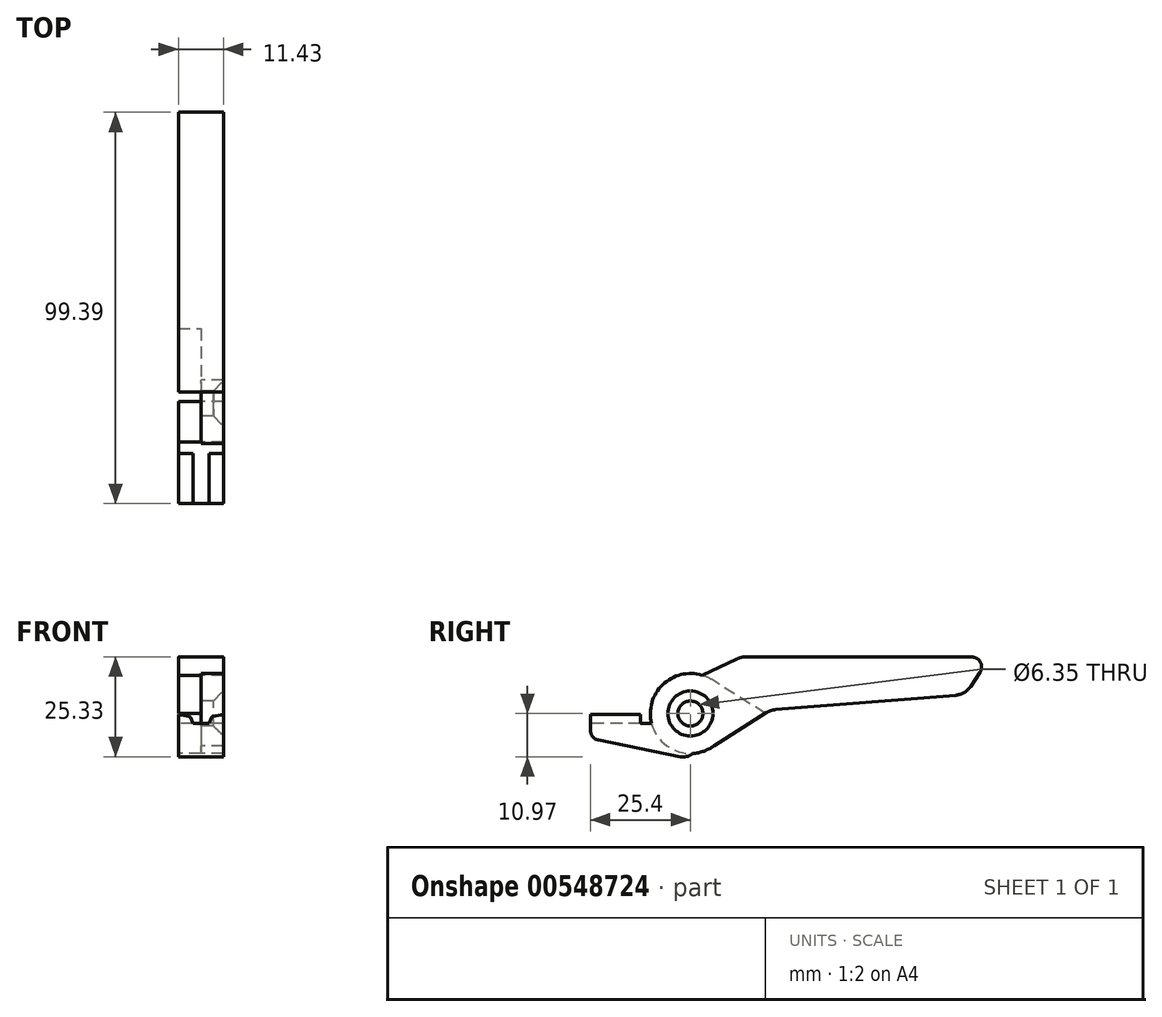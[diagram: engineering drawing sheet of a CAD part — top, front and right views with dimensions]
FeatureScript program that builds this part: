
annotation { "Feature Type Name" : "Feature", "Feature Type Description" : "" }
export const myFeature = defineFeature(function(context is Context, id is Id, definition is map)
    precondition{}
    {
        {
            var Q0;
            Q0=qCreatedBy(makeId("Right.planeOp"),FACE);
            var sketch = newSketch(context, id + "F0", { "sketchPlane" : qUnion([Q0])});
            skCircle(sketch, "E0", {"center": v(0, 0) * mm, "radius": 3.18 * mm});
            skCircle(sketch, "E1", {"center": v(0, 0) * mm, "radius": 10.16 * mm});
            skSolve(sketch);
        }
        {
            var Q0;
            Q0=qCreatedBy(makeId("Right.planeOp"),FACE);
            var sketch = newSketch(context, id + "F1", { "sketchPlane" : qUnion([Q0])});
            skLineSegment(sketch, "E2", {"start": v(9.3, 0) * mm, "end": v(10.16, 0.07) * mm});
            skLineSegment(sketch, "E3", {"start": v(69.85, 4.85) * mm, "end": v(76.2, 14.36) * mm});
            skCircle(sketch, "E4", {"center": v(0, 0) * mm, "radius": 10.16 * mm, "construction": true});
            skLineSegment(sketch, "E5", {"start": v(0, 0) * mm, "end": v(76.2, 0) * mm, "construction": true});
            skLineSegment(sketch, "E6", {"start": v(76.2, 14.36) * mm, "end": v(12.8, 14.36) * mm});
            skLineSegment(sketch, "E7", {"start": v(12.8, 14.36) * mm, "end": v(2.92, 9.73) * mm});
            skLineSegment(sketch, "E8", {"start": v(76.2, 14.36) * mm, "end": v(76.2, 0) * mm, "construction": true});
            skPoint(sketch, "E9.endSnap0", {"position": v(7.86, 12.04) * mm});
            skLineSegment(sketch, "E10", {"start": v(5.96, -8.23) * mm, "end": v(4.87, -6.63) * mm});
            skLineSegment(sketch, "E11", {"start": v(4.87, -6.63) * mm, "end": v(8.24, 1.75) * mm});
            skLineSegment(sketch, "E12", {"start": v(8.24, 1.75) * mm, "end": v(2.92, 9.73) * mm});
            skLineSegment(sketch, "E13.trimOffspring", {"start": v(20.4, 0.89) * mm, "end": v(69.85, 4.85) * mm});
            skLineSegment(sketch, "E14", {"start": v(20.4, 0.89) * mm, "end": v(5.96, -8.23) * mm});
            skSolve(sketch);
        }
        {
            var Q0;
            Q0=qSketchRegion(id+"F1",true);
            extrude(context, id + "F2", {"entities" : qUnion([Q0]), "endBound" : BoundingType.SYMMETRIC, "depth" : 11.43 * mm, "offsetDistance" : 25.4 * mm});
        }
        {
            var Q0;
            Q0=makeQuery(id+"F2.opExtrude","SWEPT_EDGE",EDGE,{"disambiguationData":[OSD([sQuery(id+"F1.wireOp",EDGE,"E6"),sQuery(id+"F1.wireOp",EDGE,"E7")])]});
            var Q1;
            Q1=makeQuery(id+"F2.opExtrude","SWEPT_EDGE",EDGE,{"disambiguationData":[OSD([sQuery(id+"F1.wireOp",EDGE,"E3"),sQuery(id+"F1.wireOp",EDGE,"E13.trimOffspring")])]});
            var Q2;
            Q2=makeQuery(id+"F2.opExtrude","SWEPT_EDGE",EDGE,{"disambiguationData":[OSD([sQuery(id+"F1.wireOp",EDGE,"E13.trimOffspring"),sQuery(id+"F1.wireOp",EDGE,"E14")])]});
            fillet(context, id + "F3", {"entities" : qUnion([Q0, Q1, Q2]), "radius" : 5.08 * mm, "tangentPropagation" : true, "allowEdgeOverflow" : false});
        }
        {
            var Q0;
            Q0=makeQuery(id+"F2.opExtrude","SWEPT_EDGE",EDGE,{"disambiguationData":[OSD([sQuery(id+"F1.wireOp",EDGE,"E3"),sQuery(id+"F1.wireOp",EDGE,"E6")])]});
            fillet(context, id + "F4", {"entities" : qUnion([Q0]), "radius" : 2.54 * mm, "tangentPropagation" : true, "allowEdgeOverflow" : false});
        }
        {
            var Q0;
            Q0=qSketchRegion(id+"F0",true);
            extrude(context, id + "F5", {"entities" : qUnion([Q0]), "operationType" : NewBodyOperationType.ADD, "depth" : 5.7 * mm, "offsetDistance" : 25.4 * mm});
        }
        {
            var Q0;
            Q0=qCreatedBy(makeId("Right.planeOp"),FACE);
            var sketch = newSketch(context, id + "F6", { "sketchPlane" : qUnion([Q0])});
            skArc(sketch, "E15", {"start": v(5.42, 8.6) * mm, "mid": v(-10.16, -0.1) * mm, "end": v(5.57, -8.5) * mm});
            skLineSegment(sketch, "E16", {"start": v(19.06, 0) * mm, "end": v(5.42, 8.6) * mm});
            skLineSegment(sketch, "E17", {"start": v(5.57, -8.5) * mm, "end": v(19.06, 0) * mm});
            skSolve(sketch);
        }
        {
            var Q0;
            Q0=qSketchRegion(id+"F6",true);
            extrude(context, id + "F7", {"entities" : qUnion([Q0]), "operationType" : NewBodyOperationType.REMOVE, "oppositeDirection" : true, "depth" : 25.4 * mm, "offsetDistance" : 25.4 * mm});
        }
        {
            var Q0;
            Q0=qCreatedBy(makeId("Right.planeOp"),FACE);
            var sketch = newSketch(context, id + "F8", { "sketchPlane" : qUnion([Q0])});
            skCircle(sketch, "E18", {"center": v(0, 0) * mm, "radius": 10.16 * mm});
            skLineSegment(sketch, "E19", {"start": v(-9.84, 2.54) * mm, "end": v(-25.4, 2.54) * mm});
            skLineSegment(sketch, "E20", {"start": v(-25.4, 2.54) * mm, "end": v(-25.4, 6.36) * mm});
            skLineSegment(sketch, "E21", {"start": v(-25.4, 6.36) * mm, "end": v(-2.53, 10.97) * mm});
            skLineSegment(sketch, "E22", {"start": v(-2.53, 10.97) * mm, "end": v(7.5, 10.97) * mm});
            skLineSegment(sketch, "E23", {"start": v(7.5, 10.97) * mm, "end": v(4.02, 9.33) * mm});
            skLineSegment(sketch, "E24", {"start": v(0, 0) * mm, "end": v(-31.38, 0) * mm, "construction": true});
            skLineSegment(sketch, "E25.MirrorCS", {"start": v(-9.84, -2.54) * mm, "end": v(-25.4, -2.54) * mm});
            skLineSegment(sketch, "E26.MirrorCS", {"start": v(-25.4, -2.54) * mm, "end": v(-25.4, -6.36) * mm});
            skLineSegment(sketch, "E27.MirrorCS", {"start": v(-25.4, -6.36) * mm, "end": v(-2.53, -10.97) * mm});
            skLineSegment(sketch, "E28.MirrorCS", {"start": v(-2.53, -10.97) * mm, "end": v(7.5, -10.97) * mm});
            skLineSegment(sketch, "E29.MirrorCS", {"start": v(7.5, -10.97) * mm, "end": v(4.02, -9.33) * mm});
            skLineSegment(sketch, "E30", {"start": v(0.54, -10.15) * mm, "end": v(0.54, -10.97) * mm});
            skSolve(sketch);
        }
        {
            var Q0;
            {var subQ0=sQuery(id+"F8.wireOp",EDGE,"E25.MirrorCS");Q0=makeQuery(id+"F8.imprint","IMPRINT",FACE,{"disambiguationData":[TD([[makeQuery(id+"F8.imprint","IMPRINT",EDGE,{"derivedFrom":subQ0}),1.0]])]});}
            extrude(context, id + "F9", {"entities" : qUnion([Q0]), "operationType" : NewBodyOperationType.ADD, "endBound" : BoundingType.SYMMETRIC, "depth" : 11.43 * mm, "offsetDistance" : 25.4 * mm});
        }
        {
            var Q0;
            Q0=makeQuery(id+"F9.opExtrude","SWEPT_EDGE",EDGE,{"disambiguationData":[OSD([sQuery(id+"F8.wireOp",EDGE,"E28.MirrorCS"),sQuery(id+"F8.wireOp",EDGE,"E30")])]});
            var Q1;
            Q1=makeQuery(id+"F9.opExtrude","SWEPT_EDGE",EDGE,{"disambiguationData":[OSD([sQuery(id+"F8.wireOp",EDGE,"E26.MirrorCS"),sQuery(id+"F8.wireOp",EDGE,"E27.MirrorCS")])]});
            fillet(context, id + "F10", {"entities" : qUnion([Q0, Q1]), "radius" : 2.54 * mm, "tangentPropagation" : true, "allowEdgeOverflow" : false});
        }
        {
            var Q0;
            Q0=makeQuery(id+"F9.opExtrude","SWEPT_FACE",FACE,{"disambiguationData":[OSD([sQuery(id+"F8.wireOp",EDGE,"E26.MirrorCS")])]});
            var sketch = newSketch(context, id + "F11", { "sketchPlane" : qUnion([Q0])});
            skLineSegment(sketch, "E31", {"start": v(2.03, -2.54) * mm, "end": v(2.76, -0.76) * mm});
            skLineSegment(sketch, "E32", {"start": v(2.76, -0.76) * mm, "end": v(5.72, -0.25) * mm});
            skLineSegment(sketch, "E33", {"start": v(5.72, -0.25) * mm, "end": v(5.72, -2.54) * mm});
            skLineSegment(sketch, "E34", {"start": v(5.72, -2.54) * mm, "end": v(2.03, -2.54) * mm});
            skLineSegment(sketch, "E35", {"start": v(0, 0) * mm, "end": v(0, -5.56) * mm, "construction": true});
            skPoint(sketch, "E35.endSnap0", {"position": v(0, -4.28) * mm});
            skLineSegment(sketch, "E36.MirrorCS", {"start": v(-2.03, -2.54) * mm, "end": v(-2.76, -0.76) * mm});
            skLineSegment(sketch, "E37.MirrorCS", {"start": v(-2.76, -0.76) * mm, "end": v(-5.72, -0.25) * mm});
            skLineSegment(sketch, "E38.MirrorCS", {"start": v(-5.72, -0.25) * mm, "end": v(-5.72, -2.54) * mm});
            skLineSegment(sketch, "E39.MirrorCS", {"start": v(-5.72, -2.54) * mm, "end": v(-2.03, -2.54) * mm});
            skSolve(sketch);
        }
        {
            var Q0;
            Q0=qSketchRegion(id+"F11",true);
            extrude(context, id + "F12", {"entities" : qUnion([Q0]), "operationType" : NewBodyOperationType.ADD, "oppositeDirection" : true, "depth" : 12.7 * mm, "offsetDistance" : 25.4 * mm});
        }
        {
            var Q0;
            Q0=makeQuery(id+"F12.opExtrude","SWEPT_EDGE",EDGE,{"disambiguationData":[OSD([sQuery(id+"F11.wireOp",EDGE,"E36.MirrorCS"),sQuery(id+"F11.wireOp",EDGE,"E37.MirrorCS")])]});
            var Q1;
            Q1=makeQuery(id+"F12.opExtrude","SWEPT_EDGE",EDGE,{"disambiguationData":[OSD([sQuery(id+"F11.wireOp",EDGE,"E31"),sQuery(id+"F11.wireOp",EDGE,"E32")])]});
            fillet(context, id + "F13", {"entities" : qUnion([Q0, Q1]), "radius" : 0.5 * mm, "tangentPropagation" : true, "allowEdgeOverflow" : false});
        }
        {
            var Q0;
            Q0=makeQuery(id+"F5.opExtrude","CAP_EDGE",EDGE,{"disambiguationData":[OSD([sQuery(id+"F0.wireOp",EDGE,"E0")])],"isStart":false});
            chamfer(context, id + "F14", {"entities" : qUnion([Q0]), "width" : 2.54 * mm, "tangentPropagation" : true});
        }
    });
